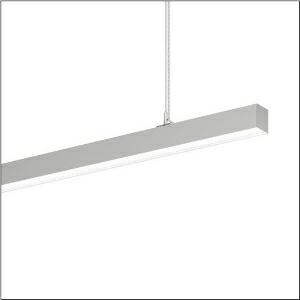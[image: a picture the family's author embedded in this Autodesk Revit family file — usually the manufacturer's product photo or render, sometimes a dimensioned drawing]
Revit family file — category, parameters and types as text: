
# Revit family: silica_21_51mx30db35sb
name_source: partatom
category: Lighting Fixtures
units: mm (PartAtom-declared; Revit-internal decimal feet)

## family parameters
Cut with Voids When Loaded = No
Host = Face
Light Source = No
Part Type = Normal
Room Calculation Point = No
Round Connector Dimension = Use Diameter
Shared = No

## types (1)
- --- (1 x LED, 5260 lm, 34.1 W, 3000K)
    Apparent Load = 34 VA
    CIE Flux Codes = 47 79 96 57 100
    Color Rendering = 80
    Color Temperature = 3000K
    Default Elevation = 1800 mm
    Description = Silica 21, office luminaire, primary optical cover: cover, of PMMA, opal, light emission: direct/indirect distribution, primary light characteristic: symmetric, installation type: suspended mounting, LED, rated luminous flux: 5.260lm, luminous efficacy: 154lm/W, light colour: 830, colour temperature: 3000K, control gear: DALI 2, with terminal, 3+2-pole, max. 2.5mm², mains connection: 220..240V, AC, 50/60Hz, rated input power: 34.1W, luminaire housing, of aluminium, metallic grey (RAL 9006), length: 1.504mm, width: 53mm, height: 53mm, protection rating (complete): IP20, insulation class (complete): insulation class I (protective earthing), certification: CE, permissible operating ambient temperature: 0..+35°C, standard: EN 50419, packaging unit: 1 piece
    Height = 53 mm
    Lamp = 1 x LED
    Lamp Light Flux = 5260 lm
    Lamp Power = 34.1 W
    Lamp count = 1
    Length = 1504 mm
    Luminous efficacy = 154 lm/W
    Manufacturer = Siteco
    ModVariant = No
    Model = 51MX30DB35SB
    Mounting Place = Ceiling
    Mounting Type = Pendant
    Number of Poles = 1
    OnlyDefault = Yes
    Power Factor = 1
    Product Name = Silica 21
    Product group = office luminaire | ceiling pendant
    ProductGroupID = 903
    Protection Class = Protection class I
    Protection Degree = IP 20
    RLX_Detail_Level = 1
    RLX_Emergency_Light_Flux = 0 lm
    RLX_Emergency_Type = 0
    RLX_Emergency_Type_DB = No
    RlxData = <blob elided: 23509 chars, md5=5bd9f9fe>
    Socket = socket
    Standby Power = 0 W
    System Light Flux = 5260 lm
    System Power = 34 W
    Type Comments = factory setting: luminous flux: 100 % | dim-lin: 254 | 233 mA
    Type Image = l_1335864.jpg
    URL = http://relux.com
    VarID = @adj_117061
    Voltage = 0 V
    Weight = 0.00 kg
    Width = 53 mm

## geometry (parser evidence)
native form markers: Blend x4, Sweep x12
no freeform markers — native parametric forms only
